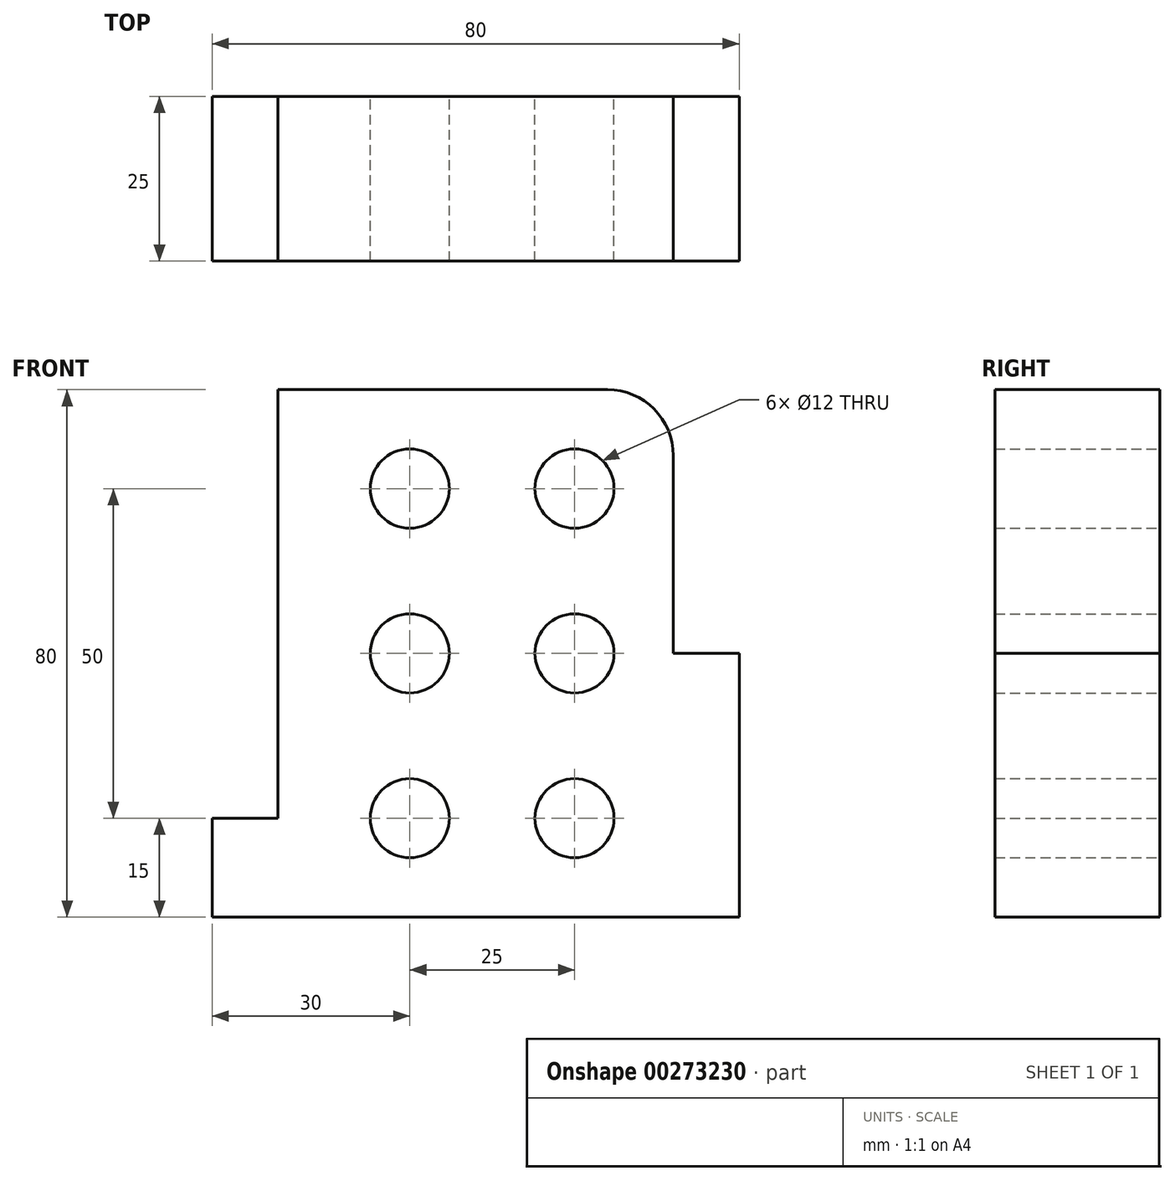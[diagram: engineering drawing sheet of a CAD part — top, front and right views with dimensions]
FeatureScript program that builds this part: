
annotation { "Feature Type Name" : "Feature", "Feature Type Description" : "" }
export const myFeature = defineFeature(function(context is Context, id is Id, definition is map)
    precondition{}
    {
        {
            var Q0;
            Q0=qCreatedBy(makeId("Front.planeOp"),FACE);
            var sketch = newSketch(context, id + "F0", { "sketchPlane" : qUnion([Q0])});
            skLineSegment(sketch, "E0", {"start": v(0, 0) * mm, "end": v(0, 15) * mm});
            skLineSegment(sketch, "E1", {"start": v(0, 15) * mm, "end": v(10, 15) * mm});
            skLineSegment(sketch, "E2", {"start": v(10, 15) * mm, "end": v(10, 80) * mm});
            skLineSegment(sketch, "E3", {"start": v(80, 0) * mm, "end": v(80, 40) * mm});
            skLineSegment(sketch, "E4", {"start": v(80, 40) * mm, "end": v(70, 40) * mm});
            skLineSegment(sketch, "E5", {"start": v(70, 40) * mm, "end": v(70, 70) * mm});
            skLineSegment(sketch, "E6", {"start": v(10, 80) * mm, "end": v(60, 80) * mm});
            skPoint(sketch, "E7.visualSharp", {"position": v(70, 80) * mm});
            skArc(sketch, "E7.filletArc", {"start": v(70, 70) * mm, "mid": v(67.07, 77.07) * mm, "end": v(60, 80) * mm});
            skLineSegment(sketch, "E8", {"start": v(0, 0) * mm, "end": v(80, 0) * mm});
            skCircle(sketch, "E9", {"center": v(30, 15) * mm, "radius": 6 * mm});
            skCircle(sketch, "E10.0.1.0", {"center": v(30, 40) * mm, "radius": 6 * mm});
            skCircle(sketch, "E10.0.2.0", {"center": v(30, 65) * mm, "radius": 6 * mm});
            skCircle(sketch, "E10.1.0.0", {"center": v(55, 15) * mm, "radius": 6 * mm});
            skCircle(sketch, "E10.1.1.0", {"center": v(55, 40) * mm, "radius": 6 * mm});
            skCircle(sketch, "E10.1.2.0", {"center": v(55, 65) * mm, "radius": 6 * mm});
            skLineSegment(sketch, "E10.direction1", {"start": v(30, 15) * mm, "end": v(55, 15) * mm, "construction": true});
            skLineSegment(sketch, "E10.direction2", {"start": v(30, 15) * mm, "end": v(30, 40) * mm, "construction": true});
            skSolve(sketch);
        }
        {
            var Q0;
            Q0 = qSketchRegion(id + "F0", true);
            extrude(context, id + "F1", {"entities" : qUnion([Q0]), "depth" : 25 * mm});
        }
    });
